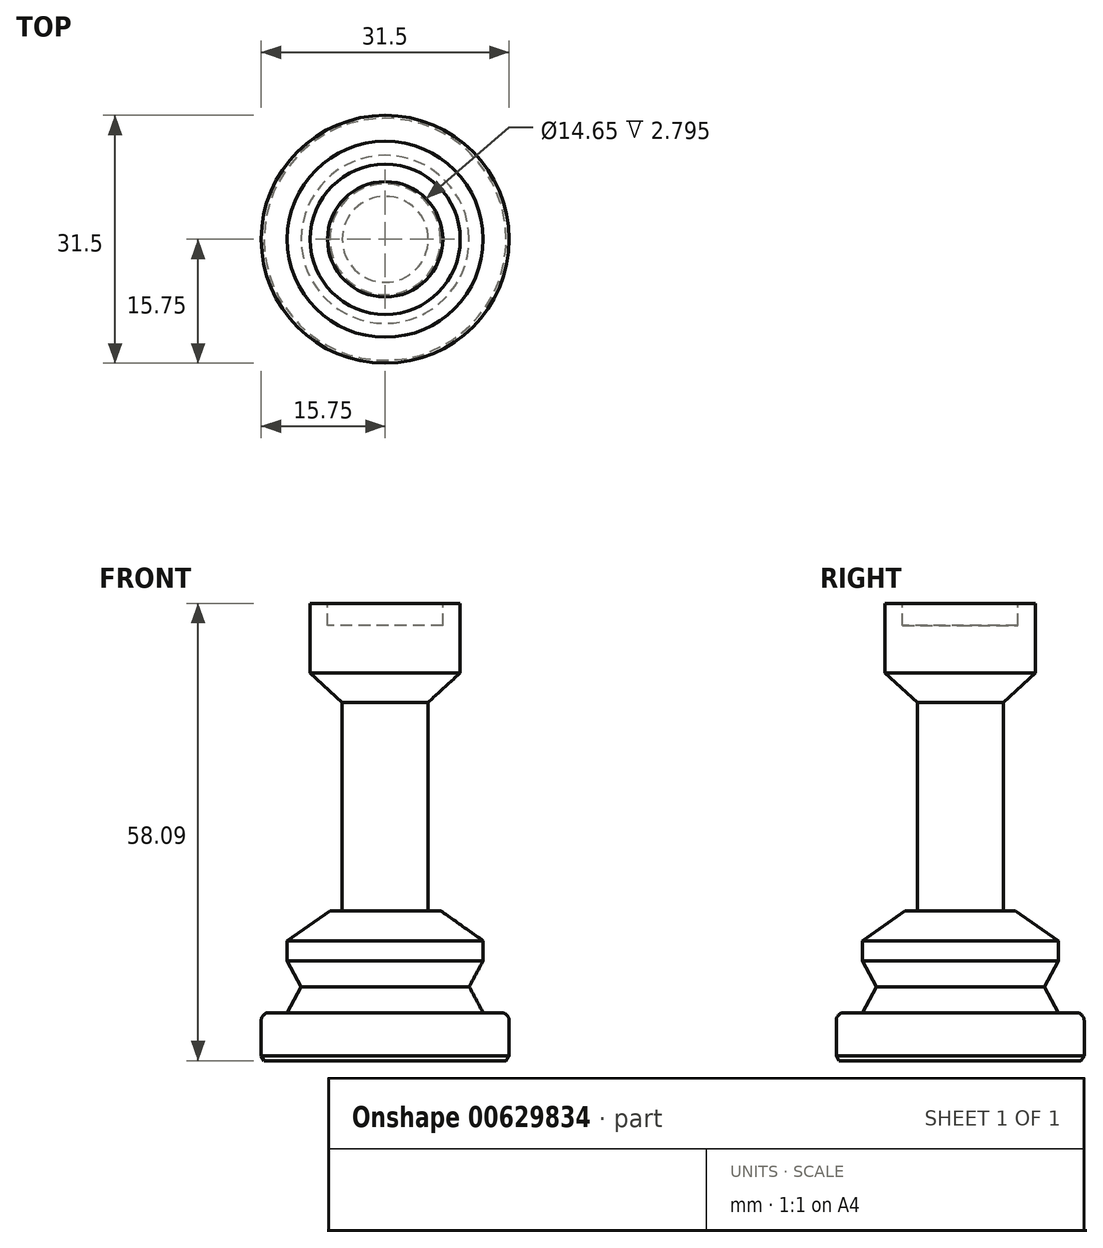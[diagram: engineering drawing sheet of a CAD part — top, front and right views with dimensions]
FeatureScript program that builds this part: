
annotation { "Feature Type Name" : "Feature", "Feature Type Description" : "" }
export const myFeature = defineFeature(function(context is Context, id is Id, definition is map)
    precondition{}
    {
        {
            var Q0;
            Q0=qCreatedBy(makeId("Front.planeOp"),FACE);
            var sketch = newSketch(context, id + "F0", { "sketchPlane" : qUnion([Q0])});
            skLineSegment(sketch, "E0.MirrorCS", {"start": v(15.37, 0) * mm, "end": v(15.75, 0.63) * mm});
            skLineSegment(sketch, "E1.MirrorCS", {"start": v(15.37, 0) * mm, "end": v(0, 0) * mm});
            skLineSegment(sketch, "E2", {"start": v(15.75, 0.64) * mm, "end": v(15.75, 5.08) * mm});
            skArc(sketch, "E3", {"start": v(15.75, 5.08) * mm, "mid": v(15.45, 5.8) * mm, "end": v(14.73, 6.1) * mm});
            skLineSegment(sketch, "E4", {"start": v(14.73, 6.1) * mm, "end": v(12.45, 6.1) * mm});
            skLineSegment(sketch, "E5", {"start": v(12.45, 12.7) * mm, "end": v(12.45, 15.24) * mm});
            skLineSegment(sketch, "E6", {"start": v(12.45, 12.7) * mm, "end": v(10.67, 9.4) * mm});
            skLineSegment(sketch, "E7", {"start": v(10.67, 9.4) * mm, "end": v(12.45, 6.1) * mm});
            skLineSegment(sketch, "E8", {"start": v(12.45, 15.24) * mm, "end": v(7.03, 19.05) * mm});
            skLineSegment(sketch, "E9", {"start": v(7.03, 19.05) * mm, "end": v(5.46, 19.05) * mm});
            skLineSegment(sketch, "E10", {"start": v(5.46, 19.05) * mm, "end": v(5.46, 45.53) * mm});
            skLineSegment(sketch, "E11", {"start": v(5.46, 45.53) * mm, "end": v(9.54, 49.27) * mm});
            skLineSegment(sketch, "E12", {"start": v(9.54, 49.27) * mm, "end": v(9.54, 58.09) * mm});
            skLineSegment(sketch, "E13", {"start": v(9.54, 58.09) * mm, "end": v(7.32, 58.09) * mm});
            skLineSegment(sketch, "E14", {"start": v(7.32, 58.09) * mm, "end": v(7.32, 55.3) * mm});
            skLineSegment(sketch, "E15", {"start": v(7.32, 55.3) * mm, "end": v(0, 55.3) * mm});
            skLineSegment(sketch, "E16", {"start": v(0, 55.3) * mm, "end": v(0, 0) * mm});
            skSolve(sketch);
        }
        {
            var Q0;
            Q0=makeQuery(id+"F0.imprint","IMPRINT",FACE,{"disambiguationData":[TD([[makeQuery(id+"F0.imprint","IMPRINT",EDGE,{"derivedFrom":sQuery(id+"F0.wireOp",EDGE,"E0.MirrorCS")}),1.0]])]});
            var Q1;
            Q1=sQuery(id+"F0.wireOp",EDGE,"E16");
            revolve(context, id + "F1", {"entities" : qUnion([Q0]), "axis" : qUnion([Q1]), "revolveType" : RevolveType.FULL});
        }
    });
